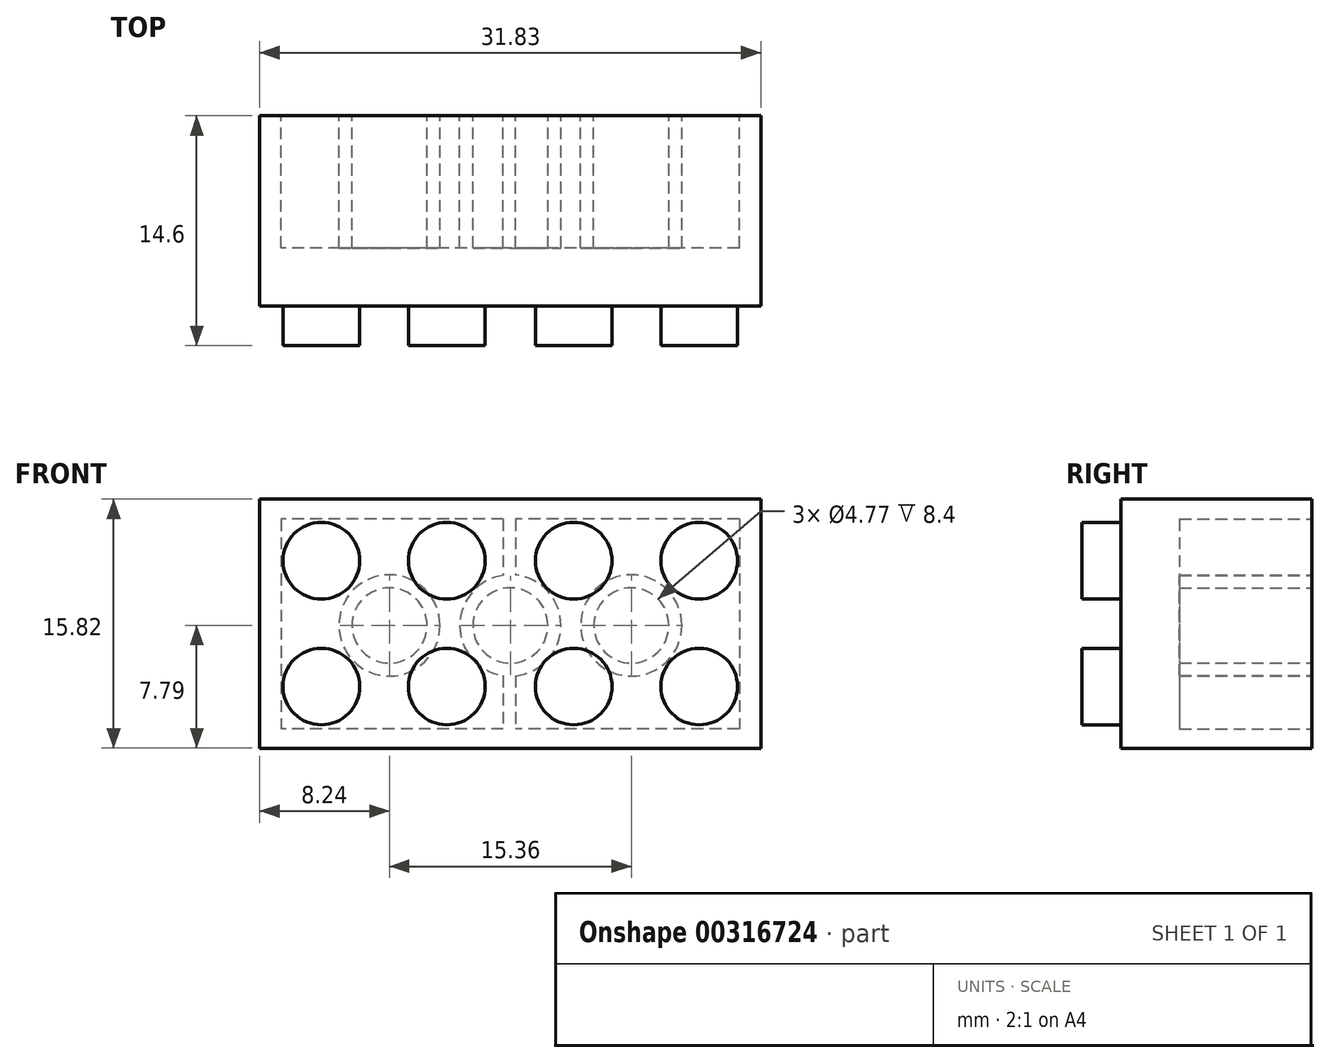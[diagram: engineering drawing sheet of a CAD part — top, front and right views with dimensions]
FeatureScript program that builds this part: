
annotation { "Feature Type Name" : "Feature", "Feature Type Description" : "" }
export const myFeature = defineFeature(function(context is Context, id is Id, definition is map)
    precondition{}
    {
        {
            var Q0;
            Q0=qCreatedBy(makeId("Front.planeOp"),FACE);
            var sketch = newSketch(context, id + "F0", { "sketchPlane" : qUnion([Q0])});
            skLineSegment(sketch, "E0.bottom", {"start": v(-21.74, 31.96) * mm, "end": v(10.09, 31.96) * mm});
            skLineSegment(sketch, "E0.top", {"start": v(-21.74, 16.14) * mm, "end": v(10.09, 16.14) * mm});
            skLineSegment(sketch, "E0.left", {"start": v(-21.74, 31.96) * mm, "end": v(-21.74, 16.14) * mm});
            skLineSegment(sketch, "E0.right", {"start": v(10.09, 31.96) * mm, "end": v(10.09, 16.14) * mm});
            skCircle(sketch, "E1", {"center": v(-17.83, 28.04) * mm, "radius": 2.44 * mm});
            skCircle(sketch, "E2", {"center": v(-9.86, 28.04) * mm, "radius": 2.43 * mm});
            skCircle(sketch, "E3", {"center": v(-1.8, 28.04) * mm, "radius": 2.43 * mm});
            skCircle(sketch, "E4", {"center": v(6.17, 28.04) * mm, "radius": 2.44 * mm});
            skCircle(sketch, "E5", {"center": v(6.17, 20.05) * mm, "radius": 2.44 * mm});
            skCircle(sketch, "E6", {"center": v(-1.8, 20.05) * mm, "radius": 2.44 * mm});
            skCircle(sketch, "E7", {"center": v(-9.86, 20.05) * mm, "radius": 2.44 * mm});
            skCircle(sketch, "E8", {"center": v(-17.83, 20.05) * mm, "radius": 2.44 * mm});
            skSolve(sketch);
        }
        {
            var Q0;
            Q0=makeQuery(id+"F0.imprint","IMPRINT",FACE,{"disambiguationData":[TD([[makeQuery(id+"F0.imprint","IMPRINT",EDGE,{"derivedFrom":sQuery(id+"F0.wireOp",EDGE,"E0.bottom")}),-1.0]])]});
            var Q1;
            Q1=makeQuery(id+"F0.imprint","IMPRINT",FACE,{"disambiguationData":[TD([[makeQuery(id+"F0.imprint","IMPRINT",EDGE,{"derivedFrom":sQuery(id+"F0.wireOp",EDGE,"E3")}),1.0]])]});
            var Q2;
            Q2=makeQuery(id+"F0.imprint","IMPRINT",FACE,{"disambiguationData":[TD([[makeQuery(id+"F0.imprint","IMPRINT",EDGE,{"derivedFrom":sQuery(id+"F0.wireOp",EDGE,"E2")}),1.0]])]});
            var Q3;
            Q3=makeQuery(id+"F0.imprint","IMPRINT",FACE,{"disambiguationData":[TD([[makeQuery(id+"F0.imprint","IMPRINT",EDGE,{"derivedFrom":sQuery(id+"F0.wireOp",EDGE,"E1")}),1.0]])]});
            var Q4;
            Q4=makeQuery(id+"F0.imprint","IMPRINT",FACE,{"disambiguationData":[TD([[makeQuery(id+"F0.imprint","IMPRINT",EDGE,{"derivedFrom":sQuery(id+"F0.wireOp",EDGE,"E8")}),1.0]])]});
            var Q5;
            Q5=makeQuery(id+"F0.imprint","IMPRINT",FACE,{"disambiguationData":[TD([[makeQuery(id+"F0.imprint","IMPRINT",EDGE,{"derivedFrom":sQuery(id+"F0.wireOp",EDGE,"E7")}),1.0]])]});
            var Q6;
            Q6=makeQuery(id+"F0.imprint","IMPRINT",FACE,{"disambiguationData":[TD([[makeQuery(id+"F0.imprint","IMPRINT",EDGE,{"derivedFrom":sQuery(id+"F0.wireOp",EDGE,"E6")}),1.0]])]});
            var Q7;
            Q7=makeQuery(id+"F0.imprint","IMPRINT",FACE,{"disambiguationData":[TD([[makeQuery(id+"F0.imprint","IMPRINT",EDGE,{"derivedFrom":sQuery(id+"F0.wireOp",EDGE,"E5")}),1.0]])]});
            var Q8;
            Q8=makeQuery(id+"F0.imprint","IMPRINT",FACE,{"disambiguationData":[TD([[makeQuery(id+"F0.imprint","IMPRINT",EDGE,{"derivedFrom":sQuery(id+"F0.wireOp",EDGE,"E4")}),1.0]])]});
            extrude(context, id + "F1", {"entities" : qUnion([Q0, Q1, Q2, Q3, Q4, Q5, Q6, Q7, Q8]), "depth" : 2.5 * mm, "hasSecondDirection" : true, "secondDirectionOppositeDirection" : true, "secondDirectionDepth" : 9.6 * mm});
        }
        {
            var Q0;
            Q0=makeQuery(id+"F0.imprint","IMPRINT",FACE,{"disambiguationData":[TD([[makeQuery(id+"F0.imprint","IMPRINT",EDGE,{"derivedFrom":sQuery(id+"F0.wireOp",EDGE,"E1")}),1.0]])]});
            var Q1;
            Q1=makeQuery(id+"F0.imprint","IMPRINT",FACE,{"disambiguationData":[TD([[makeQuery(id+"F0.imprint","IMPRINT",EDGE,{"derivedFrom":sQuery(id+"F0.wireOp",EDGE,"E8")}),1.0]])]});
            var Q2;
            Q2=makeQuery(id+"F0.imprint","IMPRINT",FACE,{"disambiguationData":[TD([[makeQuery(id+"F0.imprint","IMPRINT",EDGE,{"derivedFrom":sQuery(id+"F0.wireOp",EDGE,"E2")}),1.0]])]});
            var Q3;
            Q3=makeQuery(id+"F0.imprint","IMPRINT",FACE,{"disambiguationData":[TD([[makeQuery(id+"F0.imprint","IMPRINT",EDGE,{"derivedFrom":sQuery(id+"F0.wireOp",EDGE,"E7")}),1.0]])]});
            var Q4;
            Q4=makeQuery(id+"F0.imprint","IMPRINT",FACE,{"disambiguationData":[TD([[makeQuery(id+"F0.imprint","IMPRINT",EDGE,{"derivedFrom":sQuery(id+"F0.wireOp",EDGE,"E3")}),1.0]])]});
            var Q5;
            Q5=makeQuery(id+"F0.imprint","IMPRINT",FACE,{"disambiguationData":[TD([[makeQuery(id+"F0.imprint","IMPRINT",EDGE,{"derivedFrom":sQuery(id+"F0.wireOp",EDGE,"E6")}),1.0]])]});
            var Q6;
            Q6=makeQuery(id+"F0.imprint","IMPRINT",FACE,{"disambiguationData":[TD([[makeQuery(id+"F0.imprint","IMPRINT",EDGE,{"derivedFrom":sQuery(id+"F0.wireOp",EDGE,"E4")}),1.0]])]});
            var Q7;
            Q7=makeQuery(id+"F0.imprint","IMPRINT",FACE,{"disambiguationData":[TD([[makeQuery(id+"F0.imprint","IMPRINT",EDGE,{"derivedFrom":sQuery(id+"F0.wireOp",EDGE,"E5")}),1.0]])]});
            extrude(context, id + "F2", {"entities" : qUnion([Q0, Q1, Q2, Q3, Q4, Q5, Q6, Q7]), "operationType" : NewBodyOperationType.ADD, "depth" : 5 * mm});
        }
        {
            var Q0;
            Q0=makeQuery(id+"F1.opExtrude","CAP_FACE",FACE,{"disambiguationData":[OSD([sQuery(id+"F0.wireOp",EDGE,"E0.bottom"),sQuery(id+"F0.wireOp",EDGE,"E0.top"),sQuery(id+"F0.wireOp",EDGE,"E0.left"),sQuery(id+"F0.wireOp",EDGE,"E0.right")])],"isStart":true});
            var sketch = newSketch(context, id + "F3", { "sketchPlane" : qUnion([Q0])});
            skLineSegment(sketch, "E9.bottom", {"start": v(-8.73, 30.68) * mm, "end": v(20.38, 30.68) * mm});
            skLineSegment(sketch, "E9.top", {"start": v(-8.73, 17.36) * mm, "end": v(20.38, 17.36) * mm});
            skLineSegment(sketch, "E9.left", {"start": v(-8.73, 30.68) * mm, "end": v(-8.73, 17.36) * mm});
            skLineSegment(sketch, "E9.right", {"start": v(20.38, 30.68) * mm, "end": v(20.38, 17.36) * mm});
            skCircle(sketch, "E10", {"center": v(-1.86, 23.93) * mm, "radius": 3.21 * mm});
            skCircle(sketch, "E11", {"center": v(5.82, 23.93) * mm, "radius": 3.21 * mm});
            skCircle(sketch, "E12", {"center": v(13.5, 23.93) * mm, "radius": 3.21 * mm});
            skCircle(sketch, "E13", {"center": v(-1.86, 23.93) * mm, "radius": 2.38 * mm});
            skCircle(sketch, "E14", {"center": v(5.82, 23.93) * mm, "radius": 2.38 * mm});
            skCircle(sketch, "E15", {"center": v(13.5, 23.93) * mm, "radius": 2.38 * mm});
            skLineSegment(sketch, "E16.bottom", {"start": v(5.82, 30.68) * mm, "end": v(6.62, 30.68) * mm});
            skLineSegment(sketch, "E16.top", {"start": v(5.82, 17.36) * mm, "end": v(6.62, 17.36) * mm});
            skLineSegment(sketch, "E17", {"start": v(5.48, 30.68) * mm, "end": v(5.48, 17.36) * mm});
            skLineSegment(sketch, "E18", {"start": v(6.28, 30.68) * mm, "end": v(6.28, 17.36) * mm});
            skSolve(sketch);
        }
        {
            var Q0;
            Q0=makeQuery(id+"F3.imprint","IMPRINT",FACE,{"disambiguationData":[TD([[makeQuery(id+"F3.imprint","IMPRINT",EDGE,{"derivedFrom":sQuery(id+"F3.wireOp",EDGE,"E13")}),1.0]])]});
            var Q1;
            Q1=makeQuery(id+"F3.imprint","IMPRINT",FACE,{"disambiguationData":[TD([[makeQuery(id+"F3.imprint","IMPRINT",EDGE,{"derivedFrom":sQuery(id+"F3.wireOp",EDGE,"E14")}),1.0]])]});
            var Q2;
            Q2=makeQuery(id+"F3.imprint","IMPRINT",FACE,{"disambiguationData":[TD([[makeQuery(id+"F3.imprint","IMPRINT",EDGE,{"derivedFrom":sQuery(id+"F3.wireOp",EDGE,"E15")}),1.0]])]});
            var Q3;
            {var subQ0=sQuery(id+"F3.wireOp",EDGE,"E17");var subQ1=sQuery(id+"F3.wireOp",EDGE,"E14");var subQ2=makeQuery(id+"F3.imprint","INTERSECT",VERTEX,{"disambiguationData":[OD(0.0)],"derivedFrom":[subQ1,subQ0]});Q3=makeQuery(id+"F3.imprint","IMPRINT",FACE,{"disambiguationData":[TD([[makeQuery(id+"F3.imprint","IMPRINT",EDGE,{"disambiguationData":[TD([[subQ2,-1.0]])],"derivedFrom":subQ1}),1.0]])]});}
            var Q4;
            {var subQ0=sQuery(id+"F3.wireOp",EDGE,"E18");var subQ1=sQuery(id+"F3.wireOp",EDGE,"E14");var subQ2=makeQuery(id+"F3.imprint","INTERSECT",VERTEX,{"disambiguationData":[OD(0.0)],"derivedFrom":[subQ1,subQ0]});Q4=makeQuery(id+"F3.imprint","IMPRINT",FACE,{"disambiguationData":[TD([[makeQuery(id+"F3.imprint","IMPRINT",EDGE,{"disambiguationData":[TD([[subQ2,1.0]])],"derivedFrom":subQ1}),1.0]])]});}
            var Q5;
            {var subQ0=sQuery(id+"F3.wireOp",EDGE,"E9.left");Q5=makeQuery(id+"F3.imprint","IMPRINT",FACE,{"disambiguationData":[TD([[makeQuery(id+"F3.imprint","IMPRINT",EDGE,{"derivedFrom":subQ0}),1.0]])]});}
            var Q6;
            {var subQ0=sQuery(id+"F3.wireOp",EDGE,"E9.right");Q6=makeQuery(id+"F3.imprint","IMPRINT",FACE,{"disambiguationData":[TD([[makeQuery(id+"F3.imprint","IMPRINT",EDGE,{"derivedFrom":subQ0}),-1.0]])]});}
            extrude(context, id + "F4", {"entities" : qUnion([Q0, Q1, Q2, Q3, Q4, Q5, Q6]), "operationType" : NewBodyOperationType.REMOVE, "oppositeDirection" : true, "depth" : 8.4 * mm});
        }
    });
